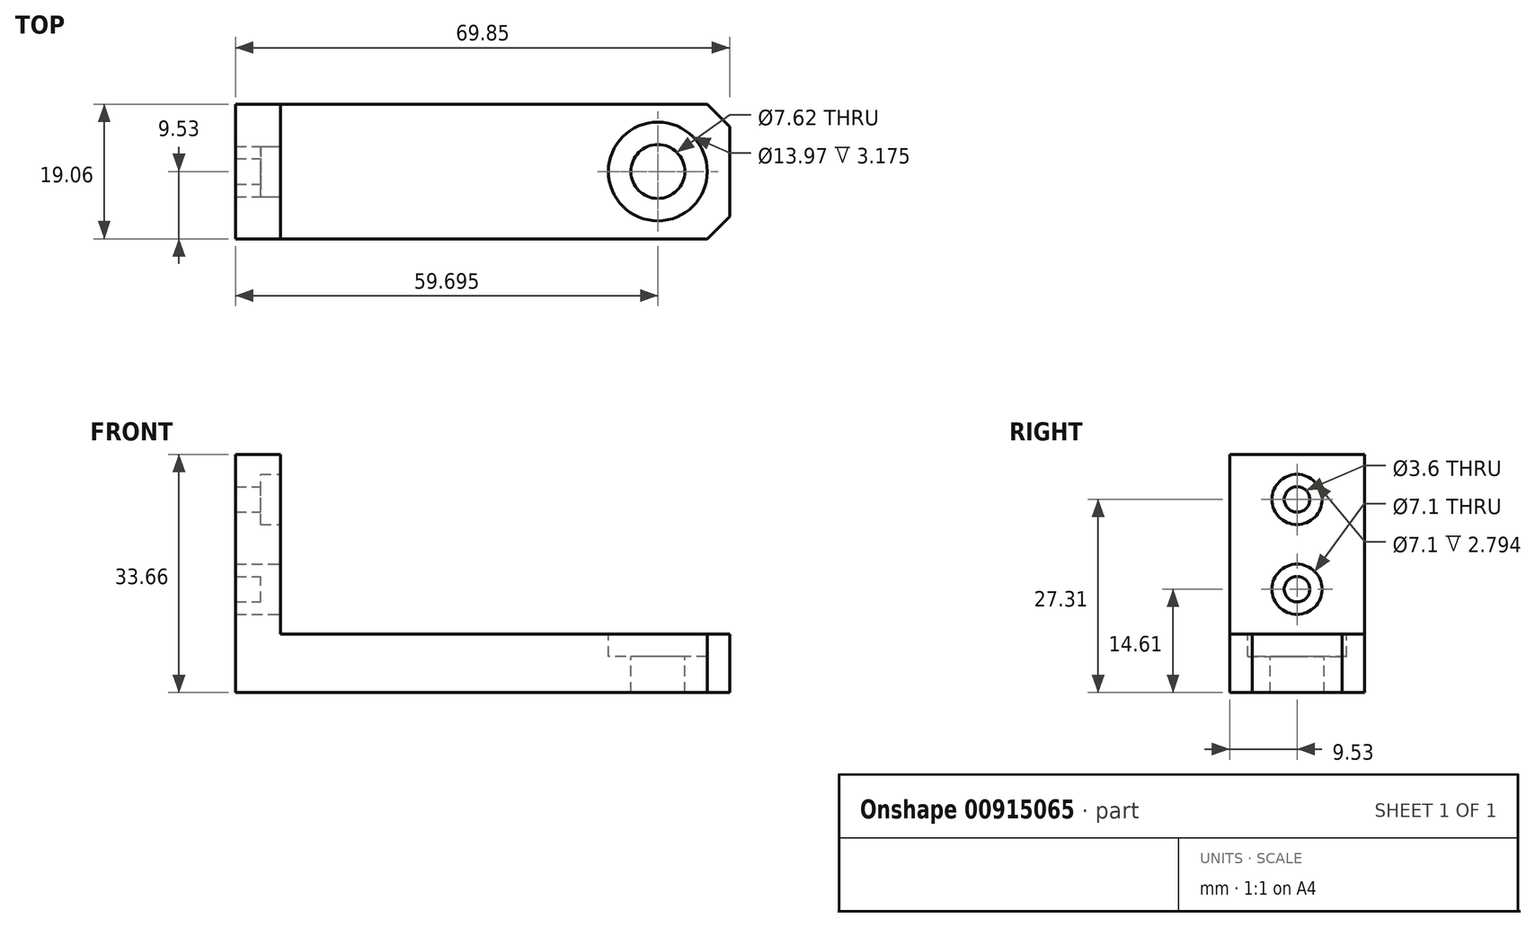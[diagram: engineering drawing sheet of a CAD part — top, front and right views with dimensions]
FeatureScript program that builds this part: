
annotation { "Feature Type Name" : "Feature", "Feature Type Description" : "" }
export const myFeature = defineFeature(function(context is Context, id is Id, definition is map)
    precondition{}
    {
        {
            var Q0;
            Q0=qCreatedBy(makeId("Top.planeOp"),FACE);
            var sketch = newSketch(context, id + "F0", { "sketchPlane" : qUnion([Q0])});
            skLineSegment(sketch, "E0.bottom", {"start": v(34.93, 9.52) * mm, "end": v(-34.93, 9.53) * mm});
            skLineSegment(sketch, "E0.top", {"start": v(34.93, -9.53) * mm, "end": v(-34.93, -9.52) * mm});
            skLineSegment(sketch, "E0.left", {"start": v(34.93, 9.52) * mm, "end": v(34.93, -9.53) * mm});
            skLineSegment(sketch, "E0.right", {"start": v(-34.93, 9.52) * mm, "end": v(-34.93, -9.52) * mm});
            skPoint(sketch, "E0.middle", {"position": v(0, 0) * mm});
            skLineSegment(sketch, "E1", {"start": v(34.93, 0) * mm, "end": v(-34.93, 0) * mm, "construction": true});
            skCircle(sketch, "E2", {"center": v(24.77, 0) * mm, "radius": 3.81 * mm});
            skLineSegment(sketch, "E3.0", {"start": v(-28.58, 9.52) * mm, "end": v(-28.58, -9.53) * mm});
            skCircle(sketch, "E4", {"center": v(24.77, 0) * mm, "radius": 6.99 * mm});
            skSolve(sketch);
        }
        {
            var Q0;
            Q0=qSketchRegion(id+"F0",true);
            var Q1;
            Q1=makeQuery(id+"F0.imprint","IMPRINT",FACE,{"disambiguationData":[TD([[makeQuery(id+"F0.imprint","IMPRINT",EDGE,{"derivedFrom":sQuery(id+"F0.wireOp",EDGE,"E2")}),-1.0]])]});
            extrude(context, id + "F1", {"entities" : qUnion([Q0, Q1]), "oppositeDirection" : true, "depth" : 8.25 * mm});
        }
        {
            var Q0;
            {var subQ0=sQuery(id+"F0.wireOp",EDGE,"E0.right");Q0=makeQuery(id+"F0.imprint","IMPRINT",FACE,{"disambiguationData":[TD([[makeQuery(id+"F0.imprint","IMPRINT",EDGE,{"derivedFrom":subQ0}),1.0]])]});}
            extrude(context, id + "F2", {"entities" : qUnion([Q0]), "operationType" : NewBodyOperationType.ADD, "depth" : 25.4 * mm});
        }
        {
            var Q0;
            Q0=makeQuery(id+"F0.imprint","IMPRINT",FACE,{"disambiguationData":[TD([[makeQuery(id+"F0.imprint","IMPRINT",EDGE,{"derivedFrom":sQuery(id+"F0.wireOp",EDGE,"E2")}),-1.0]])]});
            extrude(context, id + "F3", {"entities" : qUnion([Q0]), "operationType" : NewBodyOperationType.REMOVE, "oppositeDirection" : true, "depth" : 3.17 * mm});
        }
        {
            var Q0;
            Q0=makeQuery(id+"F2.opExtrude","SWEPT_FACE",FACE,{"disambiguationData":[OSD([sQuery(id+"F0.wireOp",EDGE,"E3.0")])]});
            var sketch = newSketch(context, id + "F4", { "sketchPlane" : qUnion([Q0])});
            skLineSegment(sketch, "E5", {"start": v(0, 25.4) * mm, "end": v(0, 0) * mm, "construction": true});
            skLineSegment(sketch, "E6", {"start": v(9.53, 12.7) * mm, "end": v(-9.53, 12.7) * mm, "construction": true});
            skCircle(sketch, "E7", {"center": v(0, 19.05) * mm, "radius": 1.8 * mm});
            skCircle(sketch, "E8.MirrorC", {"center": v(0, 6.35) * mm, "radius": 1.8 * mm});
            skCircle(sketch, "E9.0", {"center": v(0, 6.35) * mm, "radius": 3.55 * mm});
            skCircle(sketch, "E10.MirrorC", {"center": v(0, 19.05) * mm, "radius": 3.55 * mm});
            skLineSegment(sketch, "E11.bottom", {"start": v(-9.53, 25.4) * mm, "end": v(9.52, 25.4) * mm});
            skLineSegment(sketch, "E11.top", {"start": v(-9.53, 0) * mm, "end": v(9.52, 0) * mm});
            skLineSegment(sketch, "E11.left", {"start": v(-9.53, 25.4) * mm, "end": v(-9.53, 0) * mm});
            skLineSegment(sketch, "E11.right", {"start": v(9.52, 25.4) * mm, "end": v(9.52, 0) * mm});
            skSolve(sketch);
        }
        {
            var Q0;
            Q0=makeQuery(id+"F4.imprint","IMPRINT",FACE,{"disambiguationData":[TD([[makeQuery(id+"F4.imprint","IMPRINT",EDGE,{"derivedFrom":sQuery(id+"F4.wireOp",EDGE,"E8.MirrorC")}),-1.0]])]});
            var Q1;
            Q1=makeQuery(id+"F4.imprint","IMPRINT",FACE,{"disambiguationData":[TD([[makeQuery(id+"F4.imprint","IMPRINT",EDGE,{"derivedFrom":sQuery(id+"F4.wireOp",EDGE,"E7")}),1.0]])]});
            var Q2;
            {var subQ0=sQuery(id+"F0.wireOp",EDGE,"E0.right");Q2=makeQuery(id+"F2.boolean.opBoolean","MERGE",FACE,{"derivedFrom":[makeQuery(id+"F1.opExtrude","SWEPT_FACE",FACE,{"disambiguationData":[OSD([subQ0])]}),makeQuery(id+"F2.opExtrude","SWEPT_FACE",FACE,{"disambiguationData":[OSD([subQ0])]})]});}
            extrude(context, id + "F5", {"entities" : qUnion([Q0, Q1]), "operationType" : NewBodyOperationType.REMOVE, "endBound" : BoundingType.UP_TO_SURFACE, "oppositeDirection" : true, "endBoundEntityFace" : qUnion([Q2]), "depth" : 25.4 * mm});
        }
        {
            var Q0;
            Q0=makeQuery(id+"F2.opExtrude","CAP_EDGE",EDGE,{"disambiguationData":[OSD([sQuery(id+"F0.wireOp",EDGE,"E3.0")])],"isStart":true});
            var Q1;
            Q1=makeQuery(id+"F1.opExtrude","SWEPT_EDGE",EDGE,{"disambiguationData":[OSD([sQuery(id+"F0.wireOp",EDGE,"E0.bottom"),sQuery(id+"F0.wireOp",EDGE,"E0.left")])]});
            var Q2;
            Q2=makeQuery(id+"F1.opExtrude","SWEPT_EDGE",EDGE,{"disambiguationData":[OSD([sQuery(id+"F0.wireOp",EDGE,"E0.top"),sQuery(id+"F0.wireOp",EDGE,"E0.left")])]});
            chamfer(context, id + "F6", {"entities" : qUnion([Q0, Q1, Q2]), "width" : 3.17 * mm, "tangentPropagation" : true});
        }
        {
            var Q0;
            Q0=makeQuery(id+"F4.imprint","IMPRINT",FACE,{"disambiguationData":[TD([[makeQuery(id+"F4.imprint","IMPRINT",EDGE,{"derivedFrom":sQuery(id+"F4.wireOp",EDGE,"E8.MirrorC")}),1.0]])]});
            var Q1;
            Q1=makeQuery(id+"F4.imprint","IMPRINT",FACE,{"disambiguationData":[TD([[makeQuery(id+"F4.imprint","IMPRINT",EDGE,{"derivedFrom":sQuery(id+"F4.wireOp",EDGE,"E7")}),-1.0]])]});
            extrude(context, id + "F7", {"entities" : qUnion([Q0, Q1]), "operationType" : NewBodyOperationType.REMOVE, "oppositeDirection" : true, "depth" : 2.8 * mm});
        }
    });
